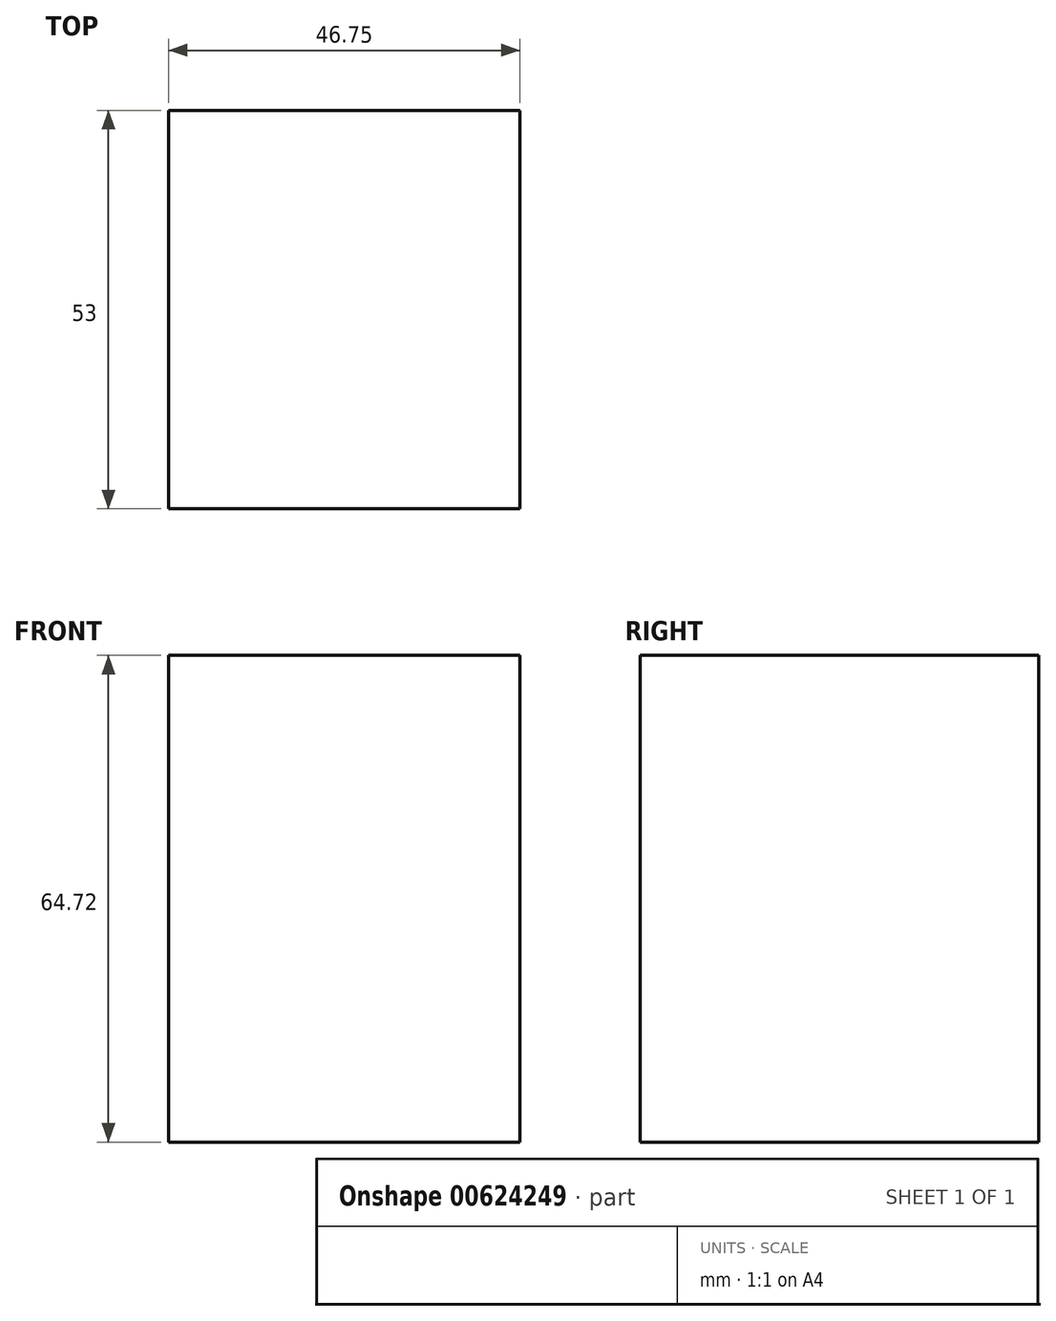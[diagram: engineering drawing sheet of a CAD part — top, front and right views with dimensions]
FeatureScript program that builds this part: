
annotation { "Feature Type Name" : "Feature", "Feature Type Description" : "" }
export const myFeature = defineFeature(function(context is Context, id is Id, definition is map)
    precondition{}
    {
        {
            var Q0;
            Q0=qCreatedBy(makeId("Front.planeOp"),FACE);
            var sketch = newSketch(context, id + "F0", { "sketchPlane" : qUnion([Q0])});
            skLineSegment(sketch, "E0.bottom", {"start": v(-63.72, -20.53) * mm, "end": v(-16.97, -20.53) * mm});
            skLineSegment(sketch, "E0.top", {"start": v(-63.72, 44.19) * mm, "end": v(-16.97, 44.19) * mm});
            skLineSegment(sketch, "E0.left", {"start": v(-63.72, -20.53) * mm, "end": v(-63.72, 44.19) * mm});
            skLineSegment(sketch, "E0.right", {"start": v(-16.97, -20.53) * mm, "end": v(-16.97, 44.19) * mm});
            skSolve(sketch);
        }
        {
            var Q0;
            Q0 = qSketchRegion(id + "F0", true);
            extrude(context, id + "F1", {"entities" : qUnion([Q0]), "depth" : 53 * mm, "offsetDistance" : 25 * mm});
        }
    });
